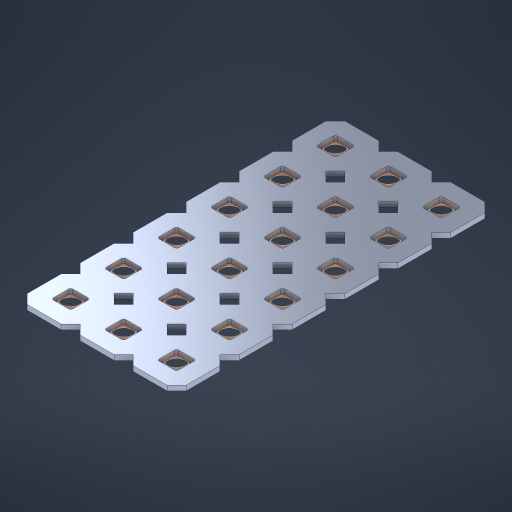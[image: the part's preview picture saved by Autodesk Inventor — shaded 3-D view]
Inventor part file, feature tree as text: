
AUTODESK INVENTOR PART (.ipt)
format: ipt  version: 2023 (Build 270158000, 158)  size: 462,848 bytes
history: native  units: in
note: dims shown in document units (in); Inventor stores cm internally (conversion verified against a paired STEP export)
features: other x19, extrude x17, sketch x2, pattern_linear x1
ambient origin geometry x8: Origin, YZ Plane, XZ Plane, XY Plane, X Axis, Y Axis, Z Axis, Center Point
bodies: Solid1 (feature_tree), Body (feature_tree)
feature tree (39):
  pattern_linear  "Rectangular Pattern1"  Spacing1=0.09in  [1 undecoded]
  sketch  "Sketch1"  dims[d1=0.5in]
  sketch  "Sketch2"  dims[d2=0.182in d3=0.09in d4=0.09in d5=0.09in d6=0.09in d7=0.09in d8=0.09in d9=0.09in d10=0.09in d11=0.02in d13=0.0in d14=0.172in d15=0.0625in d16=0.0in d19=0.5in d22=0.5in]
  other  "Srf1"
  other  "Srf126"
  other  "Srf127"
  other  "Srf128"
  other  "Srf129"
  other  "Srf130"
  other  "Srf268"
  other  "Srf269"
  other  "Srf270"
  other  "Srf271"
  other  "Srf272"
  other  "Srf273"
  other  "Srf293"
  other  "Srf294"
  other  "Srf295"
  other  "Srf296"
  other  "Srf297"
  other  "Srf298"
  other  "Circle"
  extrude  "ExtrusionSrf126"  Depth=0.09in
  extrude  "ExtrusionSrf127"  Depth=0.09in
  extrude  "ExtrusionSrf128"  Depth=0.09in
  extrude  "ExtrusionSrf129"  Depth=0.09in
  extrude  "ExtrusionSrf130"  Depth=0.09in
  extrude  "ExtrusionSrf268"  Depth=0.09in
  extrude  "ExtrusionSrf269"  Depth=0.09in
  extrude  "ExtrusionSrf270"  Depth=0.02in
  extrude  "ExtrusionSrf271"  TaperAngle=0.0deg  [1 undecoded]
  extrude  "ExtrusionSrf272"  Depth=0.5in
  extrude  "ExtrusionSrf273"  Depth=0.5in TaperAngle=0.0deg
  extrude  "ExtrusionSrf293"  Depth=0.5in
  extrude  "ExtrusionSrf294"  Depth=0.5in
  extrude  "ExtrusionSrf295"  [1 undecoded]
  extrude  "ExtrusionSrf296"  [1 undecoded]
  extrude  "ExtrusionSrf297"  [1 undecoded]
  extrude  "ExtrusionSrf298"  [1 undecoded]
note: 6 required parameter values undecoded (feature->parameter linkage not recoverable at this tier; creation-order binding heuristic only, values carry confidence <= 0.55)
